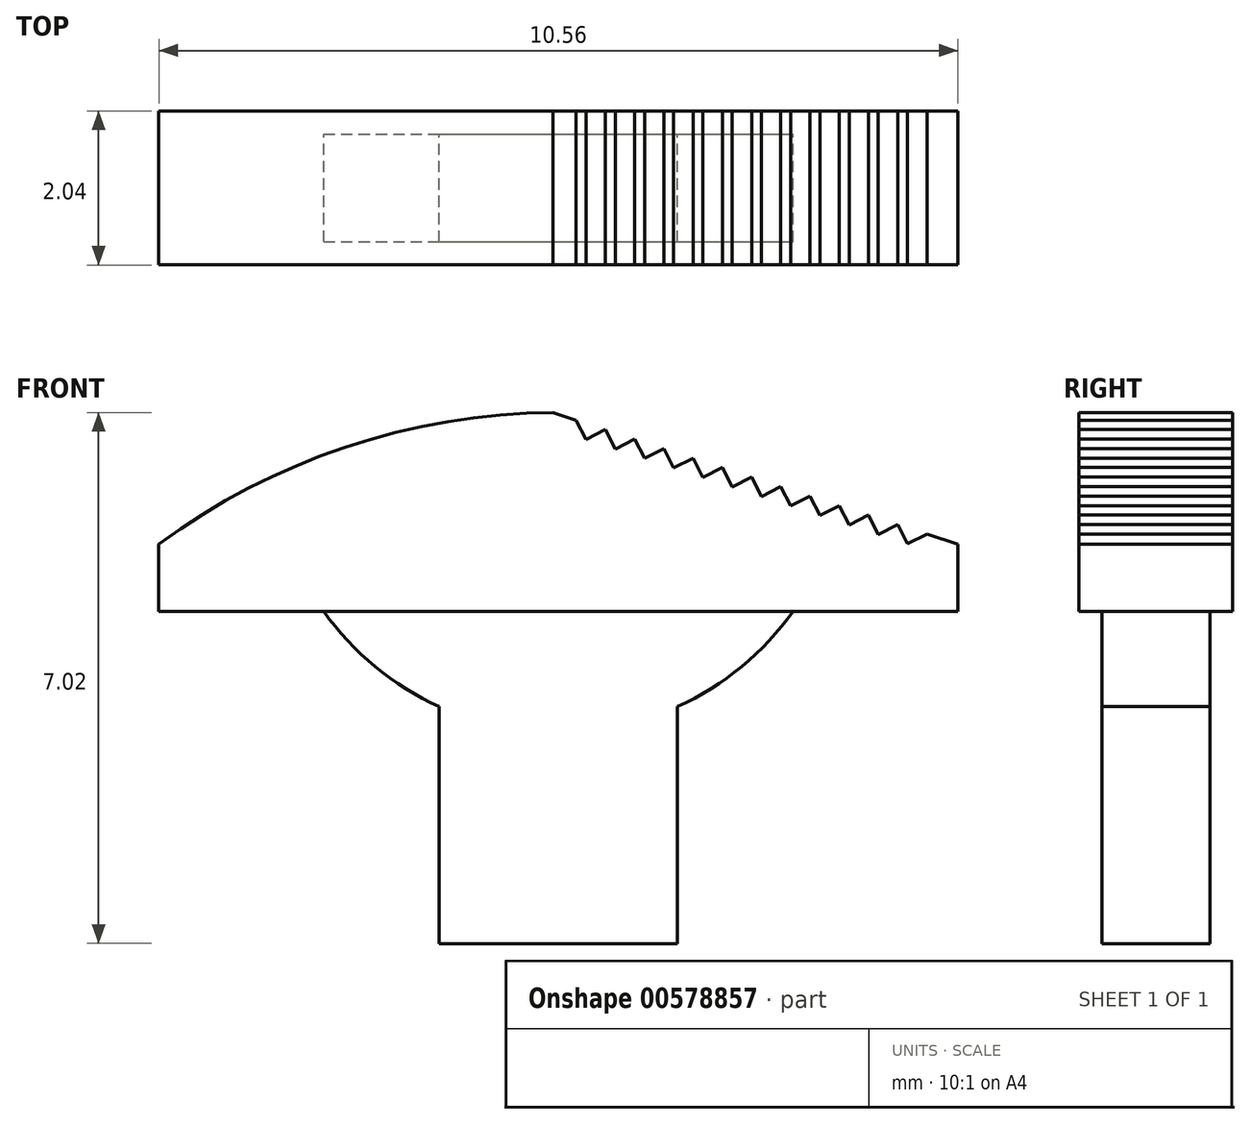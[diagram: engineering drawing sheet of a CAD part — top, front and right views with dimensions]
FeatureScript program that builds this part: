
annotation { "Feature Type Name" : "Feature", "Feature Type Description" : "" }
export const myFeature = defineFeature(function(context is Context, id is Id, definition is map)
    precondition{}
    {
        {
            var Q0;
            Q0=qCreatedBy(makeId("Front.planeOp"),FACE);
            var sketch = newSketch(context, id + "F0", { "sketchPlane" : qUnion([Q0])});
            skLineSegment(sketch, "E0.rect.top", {"start": v(-1.57, -3.5) * mm, "end": v(1.57, -3.5) * mm});
            skLineSegment(sketch, "E0.rect.left", {"start": v(-5.28, 1.8) * mm, "end": v(-5.28, 0.9) * mm});
            skLineSegment(sketch, "E0.rect.right", {"start": v(5.28, 1.8) * mm, "end": v(5.28, 0.9) * mm});
            skPoint(sketch, "E0.rect.middle", {"position": v(0, 0) * mm});
            skLineSegment(sketch, "E1", {"start": v(-5.28, 0.9) * mm, "end": v(-1.57, 0.9) * mm});
            skLineSegment(sketch, "E2.rect.left", {"start": v(-1.57, -0.36) * mm, "end": v(-1.57, -3.5) * mm});
            skLineSegment(sketch, "E2.rect.right", {"start": v(1.57, -0.36) * mm, "end": v(1.57, -3.5) * mm});
            skPoint(sketch, "E2.rect.middle", {"position": v(0, -1.3) * mm});
            skPoint(sketch, "E3.orphan", {"position": v(5.28, -3.5) * mm});
            skPoint(sketch, "E4.orphan", {"position": v(-5.28, -3.5) * mm});
            skLineSegment(sketch, "E5.trimOffspring", {"start": v(1.57, 0.9) * mm, "end": v(5.28, 0.9) * mm});
            skLineSegment(sketch, "E6", {"start": v(-1.57, 0.9) * mm, "end": v(1.57, 0.9) * mm});
            skArc(sketch, "E7", {"start": v(-3.1, 0.9) * mm, "mid": v(-2.42, 0.17) * mm, "end": v(-1.57, -0.36) * mm});
            skPoint(sketch, "E7.centerSnap0", {"position": v(0, 3.5) * mm});
            skArc(sketch, "E8.trimOffspring", {"start": v(1.57, -0.36) * mm, "mid": v(2.42, 0.17) * mm, "end": v(3.1, 0.9) * mm});
            skArc(sketch, "E9", {"start": v(-0.07, 3.53) * mm, "mid": v(-2.82, 3.07) * mm, "end": v(-5.28, 1.8) * mm});
            skPoint(sketch, "E10", {"position": v(-5.28, 1.8) * mm});
            skPoint(sketch, "E11.orphan", {"position": v(-5.28, 3.5) * mm});
            skPoint(sketch, "E12.orphan", {"position": v(5.28, 3.5) * mm});
            skLineSegment(sketch, "E13", {"start": v(5.28, 1.8) * mm, "end": v(4.87, 1.92) * mm});
            skLineSegment(sketch, "E14", {"start": v(0.23, 3.43) * mm, "end": v(0.36, 3.18) * mm});
            skLineSegment(sketch, "E15", {"start": v(0.36, 3.18) * mm, "end": v(0.62, 3.3) * mm});
            skLineSegment(sketch, "E16", {"start": v(0.62, 3.3) * mm, "end": v(0.75, 3.05) * mm});
            skLineSegment(sketch, "E17", {"start": v(0.75, 3.05) * mm, "end": v(1, 3.18) * mm});
            skLineSegment(sketch, "E18", {"start": v(1, 3.18) * mm, "end": v(1.14, 2.92) * mm});
            skLineSegment(sketch, "E19", {"start": v(1.14, 2.92) * mm, "end": v(1.4, 3.05) * mm});
            skLineSegment(sketch, "E20", {"start": v(1.4, 3.05) * mm, "end": v(1.52, 2.8) * mm});
            skLineSegment(sketch, "E21", {"start": v(1.52, 2.8) * mm, "end": v(1.78, 2.93) * mm});
            skLineSegment(sketch, "E22", {"start": v(1.78, 2.93) * mm, "end": v(1.91, 2.67) * mm});
            skLineSegment(sketch, "E23", {"start": v(1.91, 2.67) * mm, "end": v(2.17, 2.8) * mm});
            skLineSegment(sketch, "E24", {"start": v(2.17, 2.8) * mm, "end": v(2.3, 2.55) * mm});
            skLineSegment(sketch, "E25", {"start": v(2.3, 2.55) * mm, "end": v(2.55, 2.68) * mm});
            skLineSegment(sketch, "E26", {"start": v(2.55, 2.68) * mm, "end": v(2.68, 2.42) * mm});
            skLineSegment(sketch, "E27", {"start": v(2.68, 2.42) * mm, "end": v(2.94, 2.55) * mm});
            skLineSegment(sketch, "E28", {"start": v(2.94, 2.55) * mm, "end": v(3.07, 2.3) * mm});
            skLineSegment(sketch, "E29", {"start": v(3.07, 2.3) * mm, "end": v(3.33, 2.43) * mm});
            skLineSegment(sketch, "E30", {"start": v(3.33, 2.43) * mm, "end": v(3.46, 2.17) * mm});
            skLineSegment(sketch, "E31", {"start": v(3.46, 2.17) * mm, "end": v(3.71, 2.3) * mm});
            skLineSegment(sketch, "E32", {"start": v(3.71, 2.3) * mm, "end": v(3.84, 2.04) * mm});
            skLineSegment(sketch, "E33", {"start": v(3.84, 2.04) * mm, "end": v(4.1, 2.18) * mm});
            skLineSegment(sketch, "E34", {"start": v(4.1, 2.18) * mm, "end": v(4.23, 1.92) * mm});
            skLineSegment(sketch, "E35", {"start": v(4.23, 1.92) * mm, "end": v(4.49, 2.05) * mm});
            skLineSegment(sketch, "E36", {"start": v(4.49, 2.05) * mm, "end": v(4.62, 1.8) * mm});
            skLineSegment(sketch, "E37", {"start": v(4.62, 1.8) * mm, "end": v(4.87, 1.92) * mm});
            skLineSegment(sketch, "E38", {"start": v(5.28, 1.58) * mm, "end": v(-0.92, 3.6) * mm, "construction": true});
            skLineSegment(sketch, "E39.trimOffspring", {"start": v(0.23, 3.43) * mm, "end": v(-0.07, 3.53) * mm});
            skSolve(sketch);
        }
        {
            var Q0;
            {var subQ5=sQuery(id+"F0.wireOp",EDGE,"E0.rect.left");Q0=makeQuery(id+"F0.imprint","IMPRINT",FACE,{"disambiguationData":[TD([[makeQuery(id+"F0.imprint","IMPRINT",EDGE,{"derivedFrom":subQ5}),1.0]])]});}
            extrude(context, id + "F1", {"entities" : qUnion([Q0]), "endBound" : BoundingType.SYMMETRIC, "depth" : 2.03 * mm});
        }
        {
            var Q0;
            Q0=makeQuery(id+"F0.imprint","IMPRINT",FACE,{"disambiguationData":[TD([[makeQuery(id+"F0.imprint","IMPRINT",EDGE,{"derivedFrom":sQuery(id+"F0.wireOp",EDGE,"E0.rect.top")}),1.0]])]});
            extrude(context, id + "F2", {"entities" : qUnion([Q0]), "operationType" : NewBodyOperationType.ADD, "endBound" : BoundingType.SYMMETRIC, "depth" : 1.42 * mm});
        }
    });
